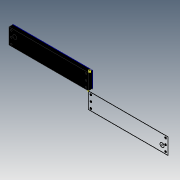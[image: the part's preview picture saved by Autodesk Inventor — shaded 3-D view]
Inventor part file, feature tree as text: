
AUTODESK INVENTOR PART (.ipt)
format: ipt  version: 2015 (Build 190159000, 159)  size: 111,104 bytes
history: native  units: mm
features: other x5, extrude x1, sketch x1, projected_geometry x1
ambient origin geometry x8: Origin, YZ Plane, XZ Plane, XY Plane, X Axis, Y Axis, Z Axis, Center Point
bodies: Body1 (feature_tree)
feature tree (8):
  other  "Blocks"
  extrude  "Extrusion3"  Depth=40.0mm
  sketch  "Sketch2"  dims[d0=200.0mm d1=40.0mm d4=4.0mm d5=4.0mm d6=5.0mm d7=5.0mm d8=4.0mm d9=20.0mm d10=100.0mm d13=10.0mm d14=15.0mm d15=15.0mm d16=10.0mm d17=0.0mm]
  other  "DXF"
  projected_geometry  "Projected Loop1"
  other  "Block1"
  other  "Block1:1"
  other  "Block1:2"
